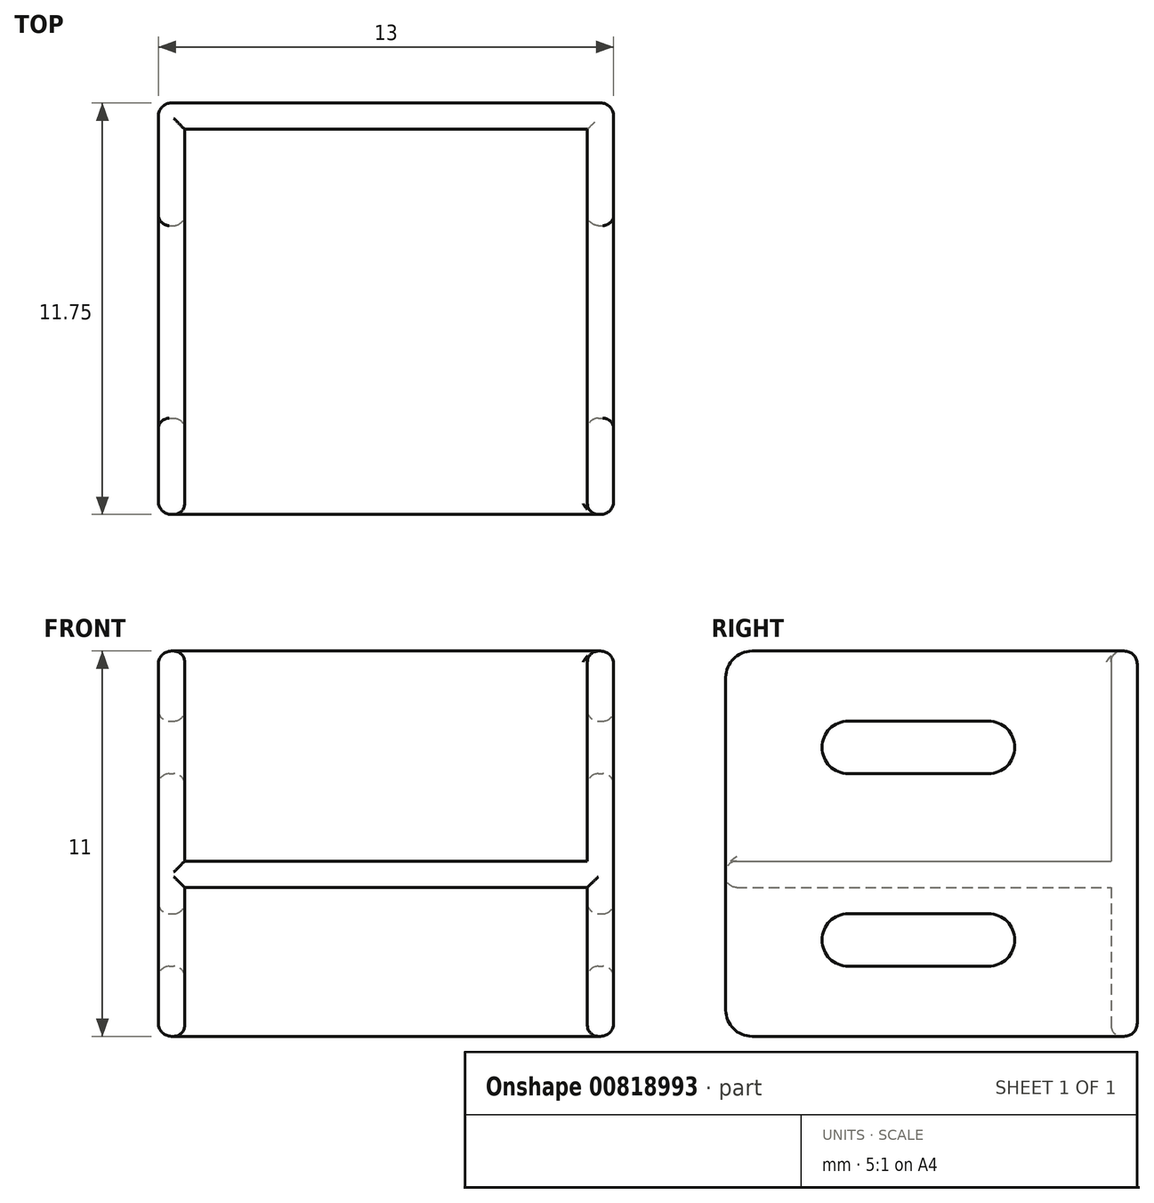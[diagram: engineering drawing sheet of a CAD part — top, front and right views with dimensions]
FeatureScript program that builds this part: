
annotation { "Feature Type Name" : "Feature", "Feature Type Description" : "" }
export const myFeature = defineFeature(function(context is Context, id is Id, definition is map)
    precondition{}
    {
        {
            var Q0;
            Q0=qCreatedBy(makeId("Front.planeOp"),FACE);
            var sketch = newSketch(context, id + "F0", { "sketchPlane" : qUnion([Q0])});
            skLineSegment(sketch, "E0.bottom", {"start": v(-6.5, 0) * mm, "end": v(6.5, 0) * mm});
            skLineSegment(sketch, "E0.top", {"start": v(-6.5, 11) * mm, "end": v(6.5, 11) * mm});
            skLineSegment(sketch, "E0.left", {"start": v(-6.5, 0) * mm, "end": v(-6.5, 11) * mm});
            skLineSegment(sketch, "E0.right", {"start": v(6.5, 0) * mm, "end": v(6.5, 11) * mm});
            skSolve(sketch);
        }
        {
            var Q0;
            Q0 = qSketchRegion(id + "F0", true);
            extrude(context, id + "F1", {"entities" : qUnion([Q0]), "oppositeDirection" : true, "depth" : .75 * mm, "offsetDistance" : 25 * mm});
        }
        {
            var Q0;
            Q0=makeQuery(id+"F1.opExtrude","CAP_FACE",FACE,{"disambiguationData":[OSD([sQuery(id+"F0.wireOp",EDGE,"E0.bottom"),sQuery(id+"F0.wireOp",EDGE,"E0.top"),sQuery(id+"F0.wireOp",EDGE,"E0.left"),sQuery(id+"F0.wireOp",EDGE,"E0.right")])],"isStart":true});
            var sketch = newSketch(context, id + "F2", { "sketchPlane" : qUnion([Q0])});
            skLineSegment(sketch, "E1.0", {"start": v(-6.5, 0) * mm, "end": v(-6.5, 11) * mm});
            skLineSegment(sketch, "E2.0", {"start": v(-6.5, 11) * mm, "end": v(-5.75, 11) * mm});
            skLineSegment(sketch, "E3.0", {"start": v(-6.5, 0) * mm, "end": v(-5.75, 0) * mm});
            skLineSegment(sketch, "E4", {"start": v(-5.75, 11) * mm, "end": v(-5.75, 5) * mm});
            skLineSegment(sketch, "E5", {"start": v(-5.75, 5) * mm, "end": v(-6, 5) * mm});
            skLineSegment(sketch, "E6", {"start": v(-6, 5) * mm, "end": v(-6, 4.25) * mm});
            skLineSegment(sketch, "E7", {"start": v(-6, 4.25) * mm, "end": v(-5.75, 4.25) * mm});
            skLineSegment(sketch, "E8", {"start": v(-5.75, 4.25) * mm, "end": v(-5.75, 0) * mm});
            skPoint(sketch, "E9.orphan", {"position": v(6.5, 11) * mm});
            skPoint(sketch, "E10.orphan", {"position": v(6.5, 0) * mm});
            skSolve(sketch);
        }
        {
            var Q0;
            Q0 = qSketchRegion(id + "F2", true);
            extrude(context, id + "F3", {"entities" : qUnion([Q0]), "depth" : 11 * mm, "offsetDistance" : 25 * mm});
        }
        {
            var Q0;
            Q0=makeQuery(id+"F1.opExtrude","CAP_FACE",FACE,{"disambiguationData":[OSD([sQuery(id+"F0.wireOp",EDGE,"E0.bottom"),sQuery(id+"F0.wireOp",EDGE,"E0.top"),sQuery(id+"F0.wireOp",EDGE,"E0.left"),sQuery(id+"F0.wireOp",EDGE,"E0.right")])],"isStart":true});
            var sketch = newSketch(context, id + "F4", { "sketchPlane" : qUnion([Q0])});
            skLineSegment(sketch, "E11", {"start": v(0, 12.29) * mm, "end": v(0, -1.26) * mm, "construction": true});
            skLineSegment(sketch, "E12.0", {"start": v(-6.5, 0) * mm, "end": v(-6.5, 11) * mm, "construction": true});
            skLineSegment(sketch, "E12.1", {"start": v(-6.5, 11) * mm, "end": v(-5.75, 11) * mm, "construction": true});
            skLineSegment(sketch, "E12.2", {"start": v(-6.5, 0) * mm, "end": v(-5.75, 0) * mm, "construction": true});
            skLineSegment(sketch, "E12.3", {"start": v(-5.75, 11) * mm, "end": v(-5.75, 5) * mm, "construction": true});
            skLineSegment(sketch, "E12.4", {"start": v(-5.75, 4.25) * mm, "end": v(-5.75, 0) * mm, "construction": true});
            skLineSegment(sketch, "E12.5", {"start": v(-6, 5) * mm, "end": v(-6, 4.25) * mm, "construction": true});
            skLineSegment(sketch, "E13.0", {"start": v(-5.75, 5) * mm, "end": v(-6, 5) * mm, "construction": true});
            skLineSegment(sketch, "E14.0", {"start": v(-6, 4.25) * mm, "end": v(-5.75, 4.25) * mm, "construction": true});
            skLineSegment(sketch, "E15.MirrorCS", {"start": v(6, 4.25) * mm, "end": v(5.75, 4.25) * mm});
            skLineSegment(sketch, "E16.MirrorCS", {"start": v(5.75, 5) * mm, "end": v(6, 5) * mm});
            skLineSegment(sketch, "E17.MirrorCS", {"start": v(6.5, 11) * mm, "end": v(5.75, 11) * mm});
            skLineSegment(sketch, "E18.MirrorCS", {"start": v(6.5, 0) * mm, "end": v(5.75, 0) * mm});
            skLineSegment(sketch, "E19.MirrorCS", {"start": v(6.5, 0) * mm, "end": v(6.5, 11) * mm});
            skLineSegment(sketch, "E20.MirrorCS", {"start": v(6, 5) * mm, "end": v(6, 4.25) * mm});
            skLineSegment(sketch, "E21.MirrorCS", {"start": v(5.75, 4.25) * mm, "end": v(5.75, 0) * mm});
            skLineSegment(sketch, "E22.MirrorCS", {"start": v(5.75, 11) * mm, "end": v(5.75, 5) * mm});
            skSolve(sketch);
        }
        {
            var Q0;
            Q0 = qSketchRegion(id + "F4", true);
            extrude(context, id + "F5", {"entities" : qUnion([Q0]), "depth" : 11 * mm, "offsetDistance" : 25 * mm});
        }
        {
            var Q0;
            Q0=makeQuery(id+"F1.opExtrude","CAP_FACE",FACE,{"disambiguationData":[OSD([sQuery(id+"F0.wireOp",EDGE,"E0.bottom"),sQuery(id+"F0.wireOp",EDGE,"E0.top"),sQuery(id+"F0.wireOp",EDGE,"E0.left"),sQuery(id+"F0.wireOp",EDGE,"E0.right")])],"isStart":true});
            var sketch = newSketch(context, id + "F6", { "sketchPlane" : qUnion([Q0])});
            skLineSegment(sketch, "E23.0", {"start": v(-6, 5) * mm, "end": v(-6, 4.25) * mm});
            skLineSegment(sketch, "E24.0", {"start": v(6, 5) * mm, "end": v(6, 4.25) * mm});
            skLineSegment(sketch, "E25", {"start": v(-6, 5) * mm, "end": v(6, 5) * mm});
            skLineSegment(sketch, "E26", {"start": v(-6, 4.25) * mm, "end": v(6, 4.25) * mm});
            skSolve(sketch);
        }
        {
            var Q0;
            Q0 = qSketchRegion(id + "F6", true);
            extrude(context, id + "F7", {"entities" : qUnion([Q0]), "depth" : 11 * mm, "offsetDistance" : 25 * mm});
        }
        {
            var Q0;
            Q0=qCreatedBy(makeId("Right.planeOp"),FACE);
            var sketch = newSketch(context, id + "F8", { "sketchPlane" : qUnion([Q0])});
            skLineSegment(sketch, "E27.bottom", {"start": v(-7.5, 9) * mm, "end": v(-3.5, 9) * mm});
            skLineSegment(sketch, "E27.top", {"start": v(-7.5, 7.5) * mm, "end": v(-3.5, 7.5) * mm});
            skLineSegment(sketch, "E28.0", {"start": v(-11, 0) * mm, "end": v(-11, 11) * mm, "construction": true});
            skLineSegment(sketch, "E29.0", {"start": v(0, 0) * mm, "end": v(0, 11) * mm, "construction": true});
            skLineSegment(sketch, "E30", {"start": v(-11, 5.5) * mm, "end": v(0, 5.5) * mm, "construction": true});
            skArc(sketch, "E31", {"start": v(-7.5, 9) * mm, "mid": v(-8.25, 8.25) * mm, "end": v(-7.5, 7.5) * mm});
            skArc(sketch, "E32", {"start": v(-3.5, 7.5) * mm, "mid": v(-2.75, 8.25) * mm, "end": v(-3.5, 9) * mm});
            skArc(sketch, "E33.MirrorCS", {"start": v(-3.5, 3.5) * mm, "mid": v(-2.75, 2.75) * mm, "end": v(-3.5, 2) * mm});
            skLineSegment(sketch, "E34.MirrorCS", {"start": v(-7.5, 2) * mm, "end": v(-3.5, 2) * mm});
            skLineSegment(sketch, "E35.MirrorCS", {"start": v(-7.5, 3.5) * mm, "end": v(-3.5, 3.5) * mm});
            skArc(sketch, "E36.MirrorCS", {"start": v(-7.5, 2) * mm, "mid": v(-8.25, 2.75) * mm, "end": v(-7.5, 3.5) * mm});
            skSolve(sketch);
        }
        {
            var Q0;
            Q0 = qSketchRegion(id + "F8", true);
            extrude(context, id + "F9", {"entities" : qUnion([Q0]), "operationType" : NewBodyOperationType.REMOVE, "endBound" : BoundingType.THROUGH_ALL, "oppositeDirection" : true, "depth" : 25 * mm, "offsetDistance" : 25 * mm, "hasSecondDirection" : true, "secondDirectionBound" : SecondDirectionBoundingType.THROUGH_ALL, "secondDirectionOppositeDirection" : false, "secondDirectionDepth" : 25 * mm});
        }
        {
            var Q0;
            Q0=makeQuery(id+"F3.opExtrude","CAP_EDGE",EDGE,{"disambiguationData":[OSD([sQuery(id+"F2.wireOp",EDGE,"E2.0")])],"isStart":false});
            var Q1;
            Q1=makeQuery(id+"F5.opExtrude","CAP_EDGE",EDGE,{"disambiguationData":[OSD([sQuery(id+"F4.wireOp",EDGE,"E17.MirrorCS")])],"isStart":false});
            var Q2;
            Q2=makeQuery(id+"F5.opExtrude","CAP_EDGE",EDGE,{"disambiguationData":[OSD([sQuery(id+"F4.wireOp",EDGE,"E18.MirrorCS")])],"isStart":false});
            var Q3;
            Q3=makeQuery(id+"F3.opExtrude","CAP_EDGE",EDGE,{"disambiguationData":[OSD([sQuery(id+"F2.wireOp",EDGE,"E3.0")])],"isStart":false});
            fillet(context, id + "F10", {"entities" : qUnion([Q0, Q1, Q2, Q3]), "radius" : .75 * mm, "tangentPropagation" : true, "allowEdgeOverflow" : false});
        }
        {
            var Q0;
            Q0=makeQuery(id+"F9.boolean.opBoolean","INTERSECT",EDGE,{"derivedFrom":[makeQuery(id+"F5.opExtrude","SWEPT_FACE",FACE,{"disambiguationData":[OSD([sQuery(id+"F4.wireOp",EDGE,"E19.MirrorCS")])]}),makeQuery(id+"F9.opExtrude","SWEPT_FACE",FACE,{"disambiguationData":[OSD([sQuery(id+"F8.wireOp",EDGE,"E32")])]})]});
            var Q1;
            Q1=makeQuery(id+"F9.boolean.opBoolean","INTERSECT",EDGE,{"derivedFrom":[makeQuery(id+"F5.opExtrude","SWEPT_FACE",FACE,{"disambiguationData":[OSD([sQuery(id+"F4.wireOp",EDGE,"E19.MirrorCS")])]}),makeQuery(id+"F9.opExtrude","SWEPT_FACE",FACE,{"disambiguationData":[OSD([sQuery(id+"F8.wireOp",EDGE,"E33.MirrorCS")])]})]});
            var Q2;
            Q2=makeQuery(id+"F9.boolean.opBoolean","INTERSECT",EDGE,{"derivedFrom":[makeQuery(id+"F5.opExtrude","SWEPT_FACE",FACE,{"disambiguationData":[OSD([sQuery(id+"F4.wireOp",EDGE,"E22.MirrorCS")])]}),makeQuery(id+"F9.opExtrude","SWEPT_FACE",FACE,{"disambiguationData":[OSD([sQuery(id+"F8.wireOp",EDGE,"E32")])]})]});
            var Q3;
            Q3=makeQuery(id+"F9.boolean.opBoolean","INTERSECT",EDGE,{"derivedFrom":[makeQuery(id+"F5.opExtrude","SWEPT_FACE",FACE,{"disambiguationData":[OSD([sQuery(id+"F4.wireOp",EDGE,"E21.MirrorCS")])]}),makeQuery(id+"F9.opExtrude","SWEPT_FACE",FACE,{"disambiguationData":[OSD([sQuery(id+"F8.wireOp",EDGE,"E33.MirrorCS")])]})]});
            var Q4;
            Q4=makeQuery(id+"F9.boolean.opBoolean","INTERSECT",EDGE,{"derivedFrom":[makeQuery(id+"F3.opExtrude","SWEPT_FACE",FACE,{"disambiguationData":[OSD([sQuery(id+"F2.wireOp",EDGE,"E4")])]}),makeQuery(id+"F9.opExtrude","SWEPT_FACE",FACE,{"disambiguationData":[OSD([sQuery(id+"F8.wireOp",EDGE,"E32")])]})]});
            var Q5;
            Q5=makeQuery(id+"F9.boolean.opBoolean","INTERSECT",EDGE,{"derivedFrom":[makeQuery(id+"F3.opExtrude","SWEPT_FACE",FACE,{"disambiguationData":[OSD([sQuery(id+"F2.wireOp",EDGE,"E8")])]}),makeQuery(id+"F9.opExtrude","SWEPT_FACE",FACE,{"disambiguationData":[OSD([sQuery(id+"F8.wireOp",EDGE,"E33.MirrorCS")])]})]});
            var Q6;
            Q6=makeQuery(id+"F9.boolean.opBoolean","INTERSECT",EDGE,{"derivedFrom":[makeQuery(id+"F3.opExtrude","SWEPT_FACE",FACE,{"disambiguationData":[OSD([sQuery(id+"F2.wireOp",EDGE,"E1.0")])]}),makeQuery(id+"F9.opExtrude","SWEPT_FACE",FACE,{"disambiguationData":[OSD([sQuery(id+"F8.wireOp",EDGE,"E32")])]})]});
            var Q7;
            Q7=makeQuery(id+"F9.boolean.opBoolean","INTERSECT",EDGE,{"derivedFrom":[makeQuery(id+"F3.opExtrude","SWEPT_FACE",FACE,{"disambiguationData":[OSD([sQuery(id+"F2.wireOp",EDGE,"E1.0")])]}),makeQuery(id+"F9.opExtrude","SWEPT_FACE",FACE,{"disambiguationData":[OSD([sQuery(id+"F8.wireOp",EDGE,"E33.MirrorCS")])]})]});
            fillet(context, id + "F11", {"entities" : qUnion([Q0, Q1, Q2, Q3, Q4, Q5, Q6, Q7]), "radius" : .31 * mm, "tangentPropagation" : true, "allowEdgeOverflow" : false});
        }
        {
            var Q0;
            Q0=makeQuery(id+"F1.opExtrude","SWEPT_BODY",BODY,{"disambiguationData":[OSD([sQuery(id+"F0.wireOp",EDGE,"E0.bottom"),sQuery(id+"F0.wireOp",EDGE,"E0.top"),sQuery(id+"F0.wireOp",EDGE,"E0.left"),sQuery(id+"F0.wireOp",EDGE,"E0.right")])]});
            var Q1;
            Q1=makeQuery(id+"F3.opExtrude","SWEPT_BODY",BODY,{"disambiguationData":[OSD([sQuery(id+"F2.wireOp",EDGE,"E1.0"),sQuery(id+"F2.wireOp",EDGE,"E2.0"),sQuery(id+"F2.wireOp",EDGE,"E3.0"),sQuery(id+"F2.wireOp",EDGE,"E4"),sQuery(id+"F2.wireOp",EDGE,"E5"),sQuery(id+"F2.wireOp",EDGE,"E6"),sQuery(id+"F2.wireOp",EDGE,"E7"),sQuery(id+"F2.wireOp",EDGE,"E8")])]});
            var Q2;
            Q2=makeQuery(id+"F5.opExtrude","SWEPT_BODY",BODY,{"disambiguationData":[OSD([sQuery(id+"F4.wireOp",EDGE,"E15.MirrorCS"),sQuery(id+"F4.wireOp",EDGE,"E16.MirrorCS"),sQuery(id+"F4.wireOp",EDGE,"E17.MirrorCS"),sQuery(id+"F4.wireOp",EDGE,"E18.MirrorCS"),sQuery(id+"F4.wireOp",EDGE,"E19.MirrorCS"),sQuery(id+"F4.wireOp",EDGE,"E20.MirrorCS"),sQuery(id+"F4.wireOp",EDGE,"E21.MirrorCS"),sQuery(id+"F4.wireOp",EDGE,"E22.MirrorCS")])]});
            var Q3;
            Q3=makeQuery(id+"F7.opExtrude","SWEPT_BODY",BODY,{"disambiguationData":[OSD([sQuery(id+"F6.wireOp",EDGE,"E23.0"),sQuery(id+"F6.wireOp",EDGE,"E24.0"),sQuery(id+"F6.wireOp",EDGE,"E25"),sQuery(id+"F6.wireOp",EDGE,"E26")])]});
            booleanBodies(context, id + "F12", {"operationType" : BooleanOperationType.UNION, "tools" : qUnion([Q0, Q1, Q2, Q3])});
        }
        {
            var Q0;
            {var subQ0=sQuery(id+"F0.wireOp",EDGE,"E0.top");Q0=makeQuery(id+"F12.opBoolean","SPLIT",FACE,{"disambiguationData":[TD([makeQuery(id+"F1.opExtrude","SWEPT_FACE",FACE,{"disambiguationData":[OSD([subQ0])]})])],"derivedFrom":makeQuery(id+"F1.opExtrude","CAP_FACE",FACE,{"disambiguationData":[OSD([sQuery(id+"F0.wireOp",EDGE,"E0.bottom"),subQ0,sQuery(id+"F0.wireOp",EDGE,"E0.left"),sQuery(id+"F0.wireOp",EDGE,"E0.right")])],"isStart":true})});}
            cPlane(context, id + "F13", {"entities" : qUnion([Q0]), "cplaneType" : CPlaneType.OFFSET, "offset" : (1 / 8) * mm, "width" : 150 * mm, "height" : 150 * mm});
        }
        {
            var Q0;
            Q0=qCreatedBy(id+"F13.planeOp",FACE);
            var sketch = newSketch(context, id + "F14", { "sketchPlane" : qUnion([Q0])});
            skLineSegment(sketch, "E37.0", {"start": v(5.63, 11) * mm, "end": v(6.06, 11) * mm});
            skArc(sketch, "E38", {"start": v(6.06, 11) * mm, "mid": v(5.84, 10.9) * mm, "end": v(5.75, 10.69) * mm});
            skPoint(sketch, "E39.orphan", {"position": v(6.5, 11) * mm});
            skLineSegment(sketch, "E40", {"start": v(5.75, 10.69) * mm, "end": v(5.63, 10.69) * mm});
            skLineSegment(sketch, "E41", {"start": v(5.63, 10.69) * mm, "end": v(5.63, 11) * mm});
            skSolve(sketch);
        }
        {
            var Q0;
            Q0 = qSketchRegion(id + "F14", true);
            var Q1;
            Q1=sQuery(id+"F14.wireOp",EDGE,"E41");
            revolve(context, id + "F15", {"operationType" : NewBodyOperationType.REMOVE, "surfaceOperationType" : NewSurfaceOperationType.NEW, "entities" : qUnion([Q0]), "axis" : qUnion([Q1]), "revolveType" : RevolveType.ONE_DIRECTION, "angle" : 90 * degree});
        }
        {
            var Q0;
            Q0=makeQuery(id+"F7.opExtrude","SWEPT_FACE",FACE,{"disambiguationData":[OSD([sQuery(id+"F6.wireOp",EDGE,"E25")])]});
            cPlane(context, id + "F16", {"entities" : qUnion([Q0]), "cplaneType" : CPlaneType.OFFSET, "offset" : (1 / 8) * mm, "width" : 150 * mm, "height" : 150 * mm});
        }
        {
            var Q0;
            Q0=qCreatedBy(id+"F16.planeOp",FACE);
            var sketch = newSketch(context, id + "F17", { "sketchPlane" : qUnion([Q0])});
            skPoint(sketch, "E42.visualSharp", {"position": v(5.75, -11) * mm});
            skArc(sketch, "E42.filletArc", {"start": v(5.75, -10.7) * mm, "mid": v(5.84, -10.9) * mm, "end": v(6.06, -11) * mm});
            skLineSegment(sketch, "E43", {"start": v(6.06, -11) * mm, "end": v(5.63, -11) * mm});
            skLineSegment(sketch, "E44", {"start": v(5.63, -10.7) * mm, "end": v(5.63, -11) * mm});
            skLineSegment(sketch, "E45", {"start": v(5.75, -10.7) * mm, "end": v(5.63, -10.7) * mm});
            skSolve(sketch);
        }
        {
            var Q0;
            Q0 = qSketchRegion(id + "F17", true);
            var Q1;
            Q1=sQuery(id+"F17.wireOp",EDGE,"E44");
            revolve(context, id + "F18", {"operationType" : NewBodyOperationType.REMOVE, "surfaceOperationType" : NewSurfaceOperationType.NEW, "entities" : qUnion([Q0]), "axis" : qUnion([Q1]), "revolveType" : RevolveType.ONE_DIRECTION, "oppositeDirection" : true, "angle" : 90 * degree});
        }
        {
            var Q0;
            Q0=qCreatedBy(makeId("Top.planeOp"),FACE);
            cPlane(context, id + "F19", {"entities" : qUnion([Q0]), "cplaneType" : CPlaneType.OFFSET, "offset" : (11 / 2) * mm, "width" : 150 * mm, "height" : 150 * mm});
        }
        {
            var Q0;
            Q0=makeQuery(id+"F7.opExtrude","SWEPT_FACE",FACE,{"disambiguationData":[OSD([sQuery(id+"F6.wireOp",EDGE,"E25")])]});
            cPlane(context, id + "F20", {"entities" : qUnion([Q0]), "cplaneType" : CPlaneType.OFFSET, "offset" : (3 / 8) * mm, "oppositeDirection" : true, "width" : 150 * mm, "height" : 150 * mm});
        }
        {
            var Q0;
            Q0=makeQuery(id+"F1.opExtrude","CAP_EDGE",EDGE,{"disambiguationData":[OSD([sQuery(id+"F0.wireOp",EDGE,"E0.top")])],"isStart":true});
            var Q1;
            Q1=makeQuery(id+"F3.opExtrude","SWEPT_EDGE",EDGE,{"disambiguationData":[OSD([sQuery(id+"F0.wireOp",EDGE,"E0.top"),sQuery(id+"F2.wireOp",EDGE,"E2.0"),sQuery(id+"F2.wireOp",EDGE,"E4")])]});
            var Q2;
            Q2=makeQuery(id+"F7.opExtrude","CAP_EDGE",EDGE,{"disambiguationData":[OSD([sQuery(id+"F6.wireOp",EDGE,"E25")])],"isStart":false});
            var Q3;
            Q3=makeQuery(id+"F1.opExtrude","CAP_EDGE",EDGE,{"disambiguationData":[OSD([sQuery(id+"F0.wireOp",EDGE,"E0.bottom")])],"isStart":true});
            var Q4;
            Q4=makeQuery(id+"F3.opExtrude","SWEPT_EDGE",EDGE,{"disambiguationData":[OSD([sQuery(id+"F0.wireOp",EDGE,"E0.bottom"),sQuery(id+"F2.wireOp",EDGE,"E3.0"),sQuery(id+"F2.wireOp",EDGE,"E8")])]});
            var Q5;
            Q5=makeQuery(id+"F7.opExtrude","CAP_EDGE",EDGE,{"disambiguationData":[OSD([sQuery(id+"F6.wireOp",EDGE,"E26")])],"isStart":false});
            var Q6;
            Q6=makeQuery(id+"F5.opExtrude","SWEPT_EDGE",EDGE,{"disambiguationData":[OSD([sQuery(id+"F0.wireOp",EDGE,"E0.bottom"),sQuery(id+"F4.wireOp",EDGE,"E18.MirrorCS"),sQuery(id+"F4.wireOp",EDGE,"E21.MirrorCS")])]});
            var Q7;
            Q7=makeQuery(id+"F5.opExtrude","SWEPT_EDGE",EDGE,{"disambiguationData":[OSD([sQuery(id+"F0.wireOp",EDGE,"E0.top"),sQuery(id+"F4.wireOp",EDGE,"E17.MirrorCS"),sQuery(id+"F4.wireOp",EDGE,"E22.MirrorCS")])]});
            fillet(context, id + "F21", {"entities" : qUnion([Q0, Q1, Q2, Q3, Q4, Q5, Q6, Q7]), "radius" : .31 * mm, "tangentPropagation" : true, "allowEdgeOverflow" : false});
        }
        {
            var Q0;
            Q0=makeQuery(id+"F12.opBoolean","MERGE",EDGE,{"derivedFrom":[makeQuery(id+"F1.opExtrude","SWEPT_EDGE",EDGE,{"disambiguationData":[OSD([sQuery(id+"F0.wireOp",EDGE,"E0.top"),sQuery(id+"F0.wireOp",EDGE,"E0.left")])]}),makeQuery(id+"F3.opExtrude","SWEPT_EDGE",EDGE,{"disambiguationData":[OSD([sQuery(id+"F2.wireOp",EDGE,"E1.0"),sQuery(id+"F2.wireOp",EDGE,"E2.0")])]})]});
            var Q1;
            Q1=makeQuery(id+"F12.opBoolean","MERGE",EDGE,{"derivedFrom":[makeQuery(id+"F1.opExtrude","SWEPT_EDGE",EDGE,{"disambiguationData":[OSD([sQuery(id+"F0.wireOp",EDGE,"E0.top"),sQuery(id+"F0.wireOp",EDGE,"E0.right")])]}),makeQuery(id+"F5.opExtrude","SWEPT_EDGE",EDGE,{"disambiguationData":[OSD([sQuery(id+"F4.wireOp",EDGE,"E17.MirrorCS"),sQuery(id+"F4.wireOp",EDGE,"E19.MirrorCS")])]})]});
            fillet(context, id + "F22", {"entities" : qUnion([Q0, Q1]), "radius" : (3 / 8) * mm, "tangentPropagation" : true, "allowEdgeOverflow" : false});
        }
        {
            var Q0;
            Q0=makeQuery(id+"F1.opExtrude","CAP_EDGE",EDGE,{"disambiguationData":[OSD([sQuery(id+"F0.wireOp",EDGE,"E0.top")])],"isStart":false});
            fillet(context, id + "F23", {"entities" : qUnion([Q0]), "radius" : (3 / 8) * mm, "tangentPropagation" : true, "allowEdgeOverflow" : false});
        }
    });
